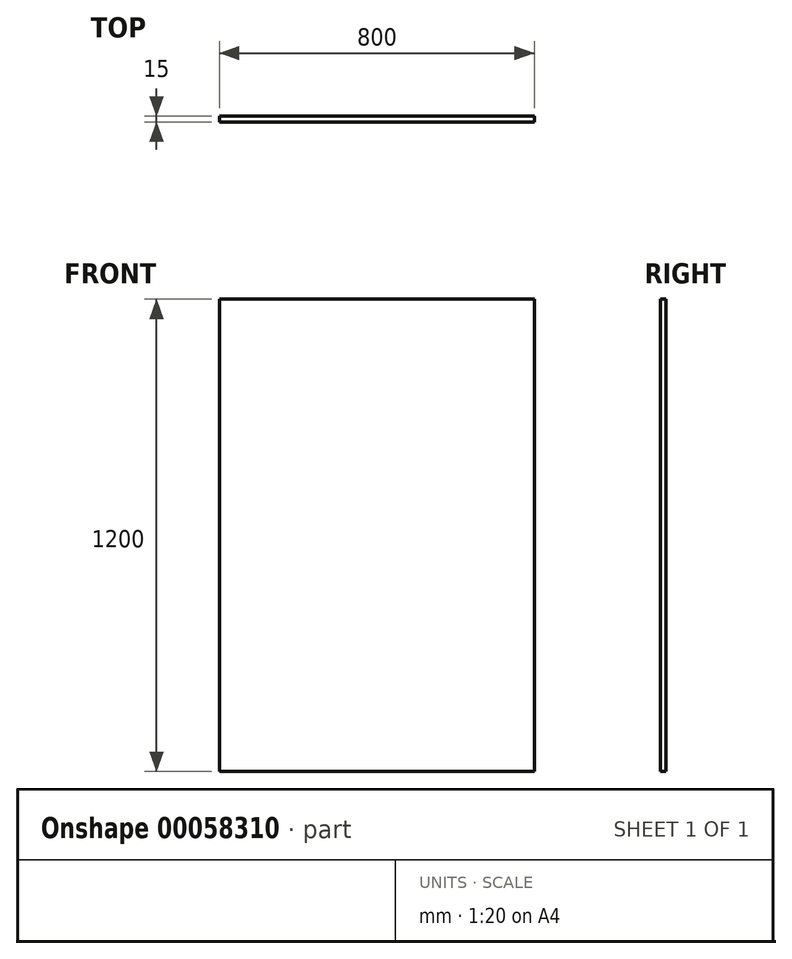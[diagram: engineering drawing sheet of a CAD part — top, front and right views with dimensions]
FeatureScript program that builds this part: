
annotation { "Feature Type Name" : "Feature", "Feature Type Description" : "" }
export const myFeature = defineFeature(function(context is Context, id is Id, definition is map)
    precondition{}
    {
        {
            var Q0;
            Q0=qCreatedBy(makeId("Front.planeOp"),FACE);
            var sketch = newSketch(context, id + "F0", { "sketchPlane" : qUnion([Q0])});
            skLineSegment(sketch, "E0.rect.bottom", {"start": v(400, -600) * mm, "end": v(-400, -600) * mm});
            skLineSegment(sketch, "E0.rect.top", {"start": v(400, 600) * mm, "end": v(-400, 600) * mm});
            skLineSegment(sketch, "E0.rect.left", {"start": v(400, -600) * mm, "end": v(400, 600) * mm});
            skLineSegment(sketch, "E0.rect.right", {"start": v(-400, -600) * mm, "end": v(-400, 600) * mm});
            skPoint(sketch, "E0.rect.middle", {"position": v(0, 0) * mm});
            skSolve(sketch);
        }
        {
            var Q0;
            Q0 = qSketchRegion(id + "F0", true);
            extrude(context, id + "F1", {"entities" : qUnion([Q0]), "depth" : 15 * mm});
        }
    });
